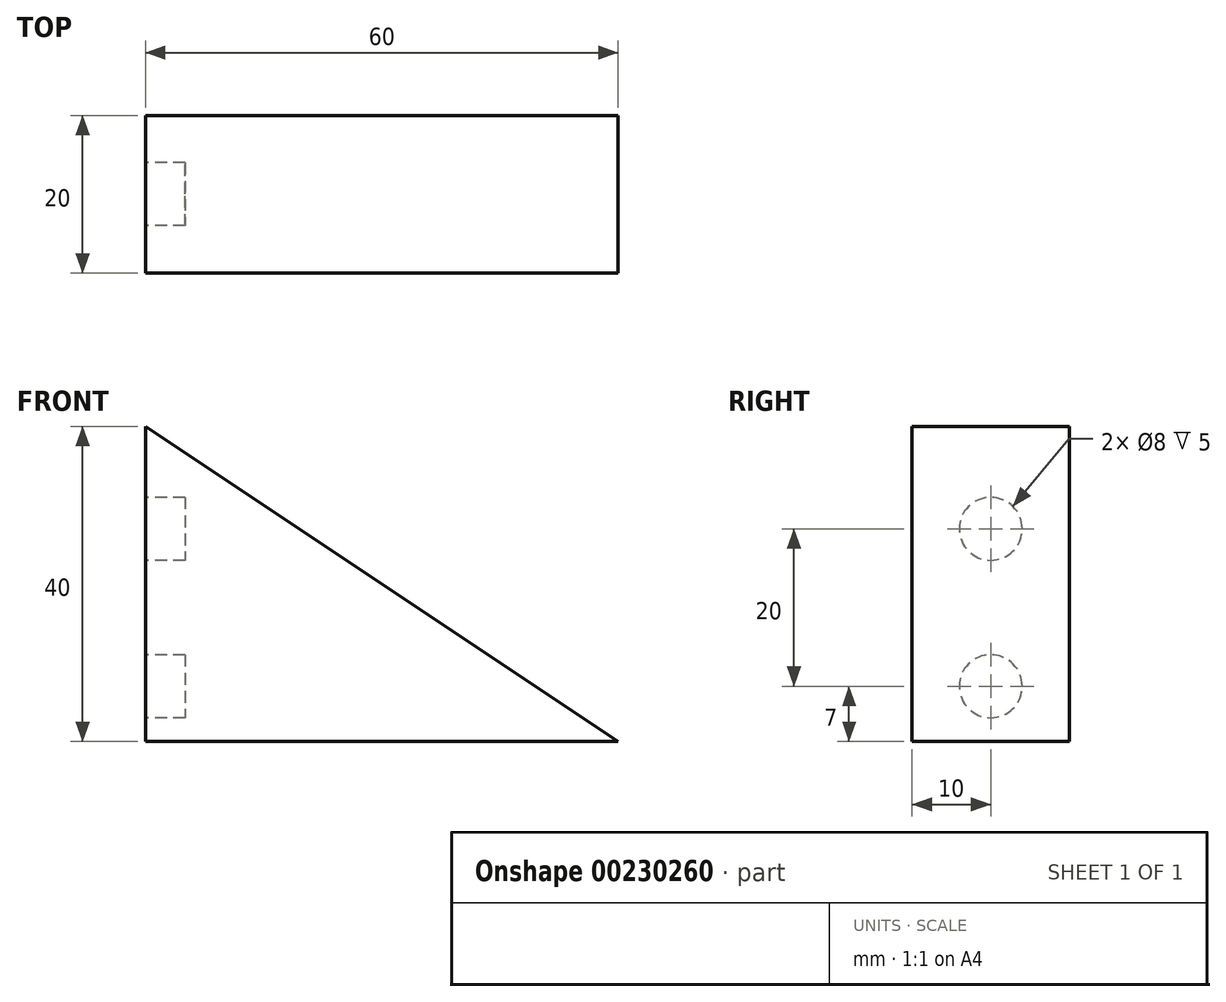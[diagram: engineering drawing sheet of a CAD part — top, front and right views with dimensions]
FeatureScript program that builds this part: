
annotation { "Feature Type Name" : "Feature", "Feature Type Description" : "" }
export const myFeature = defineFeature(function(context is Context, id is Id, definition is map)
    precondition{}
    {
        {
            var Q0;
            Q0=qCreatedBy(makeId("Front.planeOp"),FACE);
            var sketch = newSketch(context, id + "F0", { "sketchPlane" : qUnion([Q0])});
            skLineSegment(sketch, "E0", {"start": v(0, 0) * mm, "end": v(60, 0) * mm});
            skLineSegment(sketch, "E1", {"start": v(60, 0) * mm, "end": v(0, 40) * mm});
            skLineSegment(sketch, "E2", {"start": v(0, 40) * mm, "end": v(0, 0) * mm});
            skSolve(sketch);
        }
        {
            var Q0;
            Q0=makeQuery(id+"F0.imprint","IMPRINT",FACE,{"disambiguationData":[TD([[makeQuery(id+"F0.imprint","IMPRINT",EDGE,{"derivedFrom":sQuery(id+"F0.wireOp",EDGE,"E0")}),1.0]])]});
            extrude(context, id + "F1", {"entities" : qUnion([Q0]), "depth" : 20 * mm});
        }
        {
            var Q0;
            Q0=makeQuery(id+"F1.opExtrude","SWEPT_FACE",FACE,{"disambiguationData":[OSD([sQuery(id+"F0.wireOp",EDGE,"E2")])]});
            var sketch = newSketch(context, id + "F2", { "sketchPlane" : qUnion([Q0])});
            skCircle(sketch, "E3", {"center": v(10, 7) * mm, "radius": 4 * mm});
            skCircle(sketch, "E4", {"center": v(10, 27) * mm, "radius": 4 * mm});
            skSolve(sketch);
        }
        {
            var Q0;
            Q0=makeQuery(id+"F2.imprint","IMPRINT",FACE,{"disambiguationData":[TD([[makeQuery(id+"F2.imprint","IMPRINT",EDGE,{"derivedFrom":sQuery(id+"F2.wireOp",EDGE,"E3")}),1.0]])]});
            var Q1;
            Q1=makeQuery(id+"F2.imprint","IMPRINT",FACE,{"disambiguationData":[TD([[makeQuery(id+"F2.imprint","IMPRINT",EDGE,{"derivedFrom":sQuery(id+"F2.wireOp",EDGE,"E4")}),1.0]])]});
            extrude(context, id + "F3", {"entities" : qUnion([Q0, Q1]), "operationType" : NewBodyOperationType.REMOVE, "oppositeDirection" : true, "depth" : 5 * mm});
        }
    });
